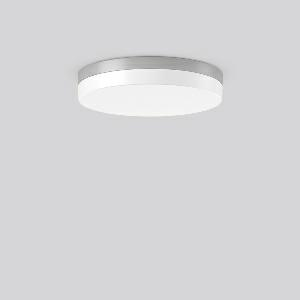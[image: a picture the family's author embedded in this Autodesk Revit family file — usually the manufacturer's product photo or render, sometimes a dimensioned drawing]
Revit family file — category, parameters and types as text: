
# Revit family: flat_slim_round_312675_004_19_11cc
name_source: partatom
category: Lighting Fixtures
units: mm (PartAtom-declared; Revit-internal decimal feet)

## family parameters
Cut with Voids When Loaded = No
Host = Face
Light Source = No
Part Type = Normal
Room Calculation Point = No
Round Connector Dimension = Use Diameter
Shared = No

## types (1)
- MultiLumen 1 830 (1 x LED Modul 830, 2450 lm, 3000)
    Apparent Load = 25 VA
    CIE Flux Codes = 40 70 90 84 100
    Color Rendering = 80
    Color Temperature = 3000
    Default Elevation = 1800 mm
    Height = 75 mm
    Lamp = 1 x LED Modul 830
    Lamp Light Flux = 2450 lm
    Lamp count = 1
    Length = 400 mm
    Lifetime = 50000 h
    Luminous efficacy = 98 lm/W
    Manufacturer = RZB
    ModVariant = No
    Model = 312675.004.19
    Mounting Place = Ceiling
    Mounting Type = Surface mounted
    Number of Poles = 1
    OnlyDefault = Yes
    Power Factor = 1
    Product Name = FLAT SLIM round
    Product group = Surface mounted ceiling and wall luminaires
    ProductGroupID = 305
    Protection Class = Protection class I
    Protection Degree = Degree of protection
    RLX_Detail_Level = 1
    RLX_Emergency_Light_Flux = 0 lm
    RLX_Emergency_Type = 0
    RLX_Emergency_Type_DB = No
    RlxData = <blob elided: 20829 chars, md5=0d6bd325>
    Socket = socket
    Standby Power = 0 W
    System Light Flux = 2450 lm
    System Power = 25 W
    Type Comments = MultiLumen 1 830
    Type Image = 312631.004.jpg
    URL = http://relux.com
    VarID = multilumen_1_830
    Voltage = 0 V
    Weight = 0.00 kg
    Width = 0 mm  [stored 0 ft]

note: [stored X ft] marks values corroborated as IEEE doubles in the binary element streams (Revit-internal decimal feet)

## geometry (parser evidence)
native form markers: Blend x4, Sweep x15
no freeform markers — native parametric forms only
